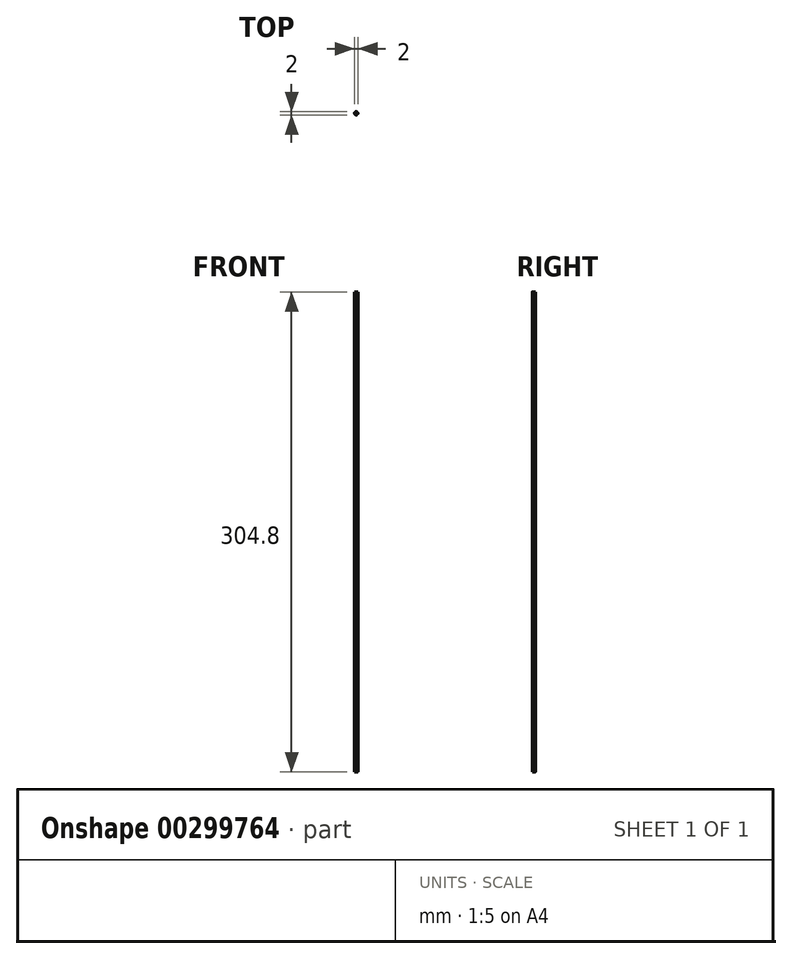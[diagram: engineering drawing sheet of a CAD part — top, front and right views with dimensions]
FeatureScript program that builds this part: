
annotation { "Feature Type Name" : "Feature", "Feature Type Description" : "" }
export const myFeature = defineFeature(function(context is Context, id is Id, definition is map)
    precondition{}
    {
        {
            var Q0;
            Q0=qCreatedBy(makeId("Top.planeOp"),FACE);
            var sketch = newSketch(context, id + "F0", { "sketchPlane" : qUnion([Q0])});
            skCircle(sketch, "E0", {"center": v(0, 0) * mm, "radius": 1 * mm});
            skSolve(sketch);
        }
        {
            var Q0;
            Q0 = qSketchRegion(id + "F0", true);
            extrude(context, id + "F1", {"entities" : qUnion([Q0]), "depth" : 304.8 * mm});
        }
    });
